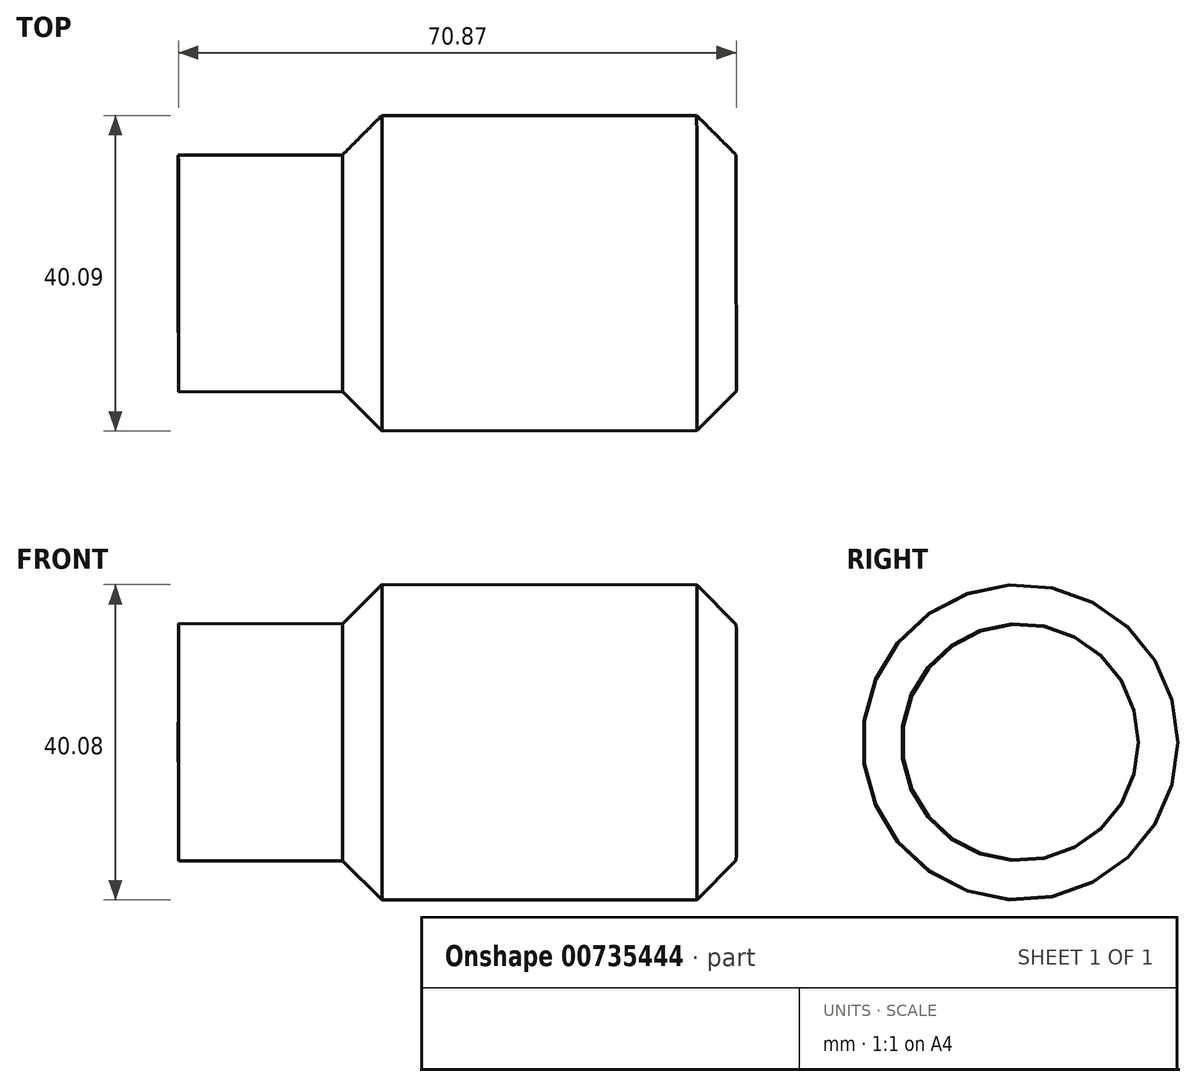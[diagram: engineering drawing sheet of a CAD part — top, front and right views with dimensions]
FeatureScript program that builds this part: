
annotation { "Feature Type Name" : "Feature", "Feature Type Description" : "" }
export const myFeature = defineFeature(function(context is Context, id is Id, definition is map)
    precondition{}
    {
        {
            var Q0;
            Q0=qCreatedBy(makeId("Top.planeOp"),FACE);
            var sketch = newSketch(context, id + "F0", { "sketchPlane" : qUnion([Q0])});
            skLineSegment(sketch, "E0", {"start": v(-17.64, 20.07) * mm, "end": v(22.36, 20.07) * mm});
            skLineSegment(sketch, "E1", {"start": v(27.36, 0.07) * mm, "end": v(27.36, 15.07) * mm});
            skLineSegment(sketch, "E2", {"start": v(-22.64, 15.07) * mm, "end": v(-17.64, 20.07) * mm});
            skLineSegment(sketch, "E3", {"start": v(22.36, 20.07) * mm, "end": v(27.36, 15.07) * mm});
            skLineSegment(sketch, "E4.MirrorCS", {"start": v(-22.64, -14.93) * mm, "end": v(-17.64, -19.93) * mm});
            skLineSegment(sketch, "E5.MirrorCS", {"start": v(22.36, -19.93) * mm, "end": v(27.36, -14.93) * mm});
            skLineSegment(sketch, "E6.MirrorCS", {"start": v(27.36, 0.07) * mm, "end": v(27.36, -14.93) * mm});
            skLineSegment(sketch, "E7.MirrorCS", {"start": v(-17.64, -19.93) * mm, "end": v(22.36, -19.93) * mm});
            skLineSegment(sketch, "E8", {"start": v(-22.64, 15.07) * mm, "end": v(-43.48, 15.07) * mm});
            skLineSegment(sketch, "E9", {"start": v(-43.48, 15.07) * mm, "end": v(-43.48, -14.93) * mm});
            skLineSegment(sketch, "E10", {"start": v(-43.48, -14.93) * mm, "end": v(-22.64, -14.93) * mm});
            skLineSegment(sketch, "E11", {"start": v(27.36, 0.07) * mm, "end": v(-43.48, 0) * mm});
            skSolve(sketch);
        }
        {
            var Q0;
            {var subQ0=sQuery(id+"F0.wireOp",EDGE,"E2");Q0=makeQuery(id+"F0.imprint","IMPRINT",FACE,{"disambiguationData":[TD([[makeQuery(id+"F0.imprint","IMPRINT",EDGE,{"derivedFrom":subQ0}),-1.0]])]});}
            var Q1;
            {var subQ0=sQuery(id+"F0.wireOp",EDGE,"E0");Q1=makeQuery(id+"F0.imprint","IMPRINT",FACE,{"disambiguationData":[TD([[makeQuery(id+"F0.imprint","IMPRINT",EDGE,{"derivedFrom":subQ0}),-1.0]])]});}
            var Q2;
            {var subQ0=sQuery(id+"F0.wireOp",EDGE,"E3");Q2=makeQuery(id+"F0.imprint","IMPRINT",FACE,{"disambiguationData":[TD([[makeQuery(id+"F0.imprint","IMPRINT",EDGE,{"derivedFrom":subQ0}),-1.0]])]});}
            var Q3;
            Q3=makeQuery(id+"F0.imprint","IMPRINT",FACE,{"disambiguationData":[TD([[makeQuery(id+"F0.imprint","IMPRINT",EDGE,{"derivedFrom":sQuery(id+"F0.wireOp",EDGE,"E1")}),1.0]])]});
            var Q4;
            Q4=sQuery(id+"F0.wireOp",EDGE,"E11");
            revolve(context, id + "F1", {"surfaceOperationType" : NewSurfaceOperationType.NEW, "entities" : qUnion([Q0, Q1, Q2, Q3]), "axis" : qUnion([Q4]), "revolveType" : RevolveType.FULL});
        }
    });
